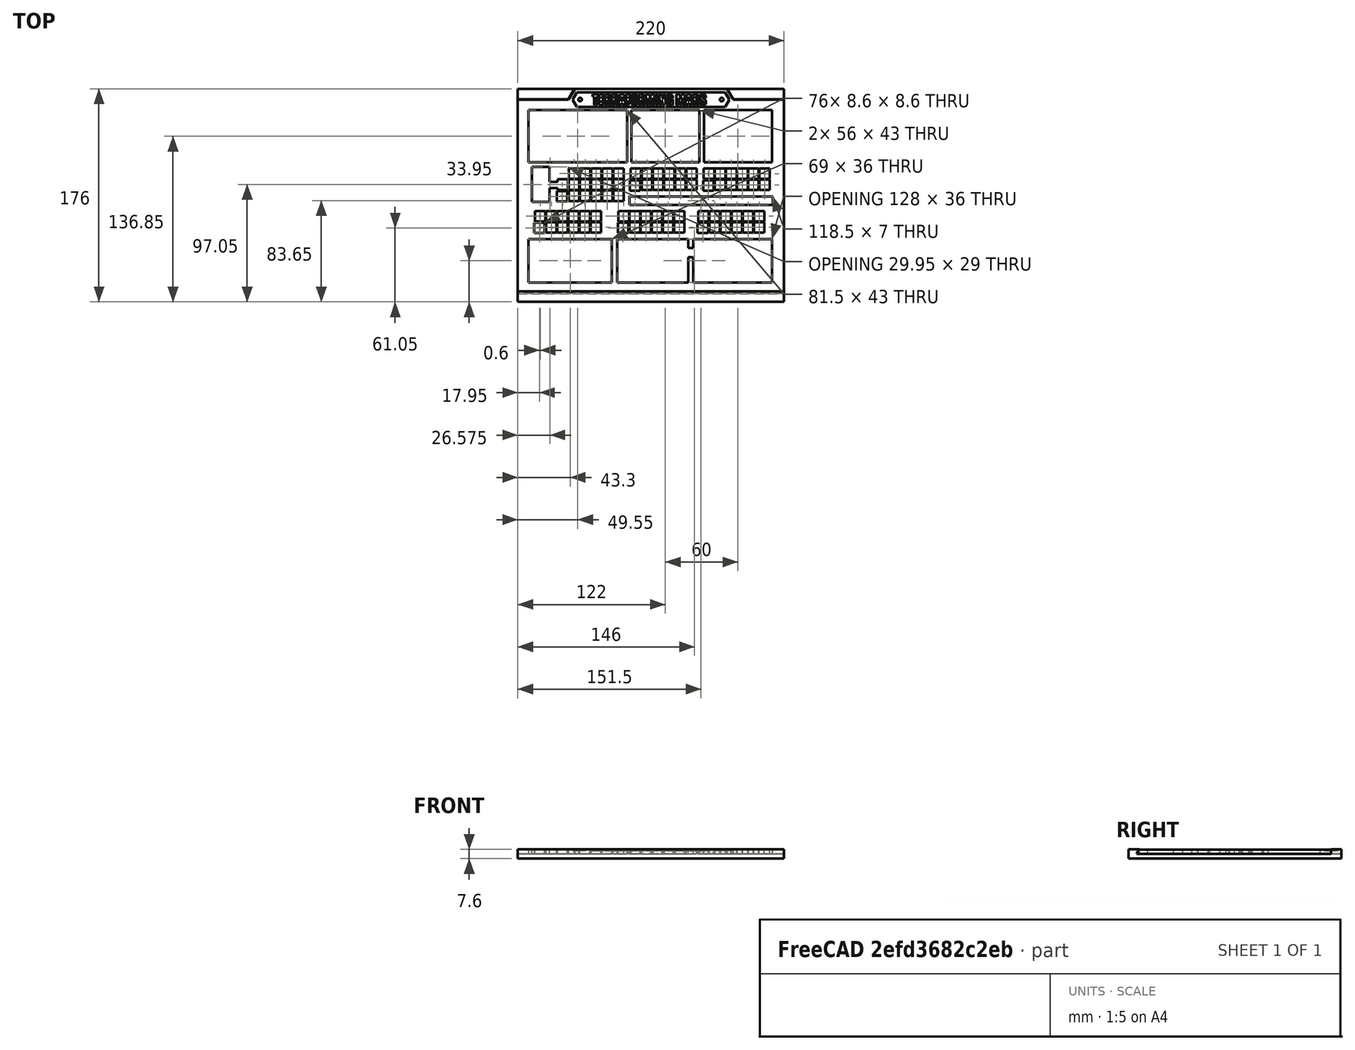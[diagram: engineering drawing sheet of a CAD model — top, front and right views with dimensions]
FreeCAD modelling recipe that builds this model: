
FCSTD DOCUMENT  (FreeCAD 1.0R39109 (Git))
Label: overlay-full-v8
License: All rights reserved
LicenseURL: https://en.wikipedia.org/wiki/All_rights_reserved
objects: Sketcher::SketchObject×11, PartDesign::Pad×9, PartDesign::Pocket×7, Part::Feature×2, PartDesign::Body×2, Mesh::Feature×1, Part::Refine×1, PartDesign::FeatureBase×1, Part::Part2DObjectPython×1, Part::Extrusion×1
note: 79 computed .brp shape members not serialized (recipe doc carries the construction recipe); baked Part::Feature solids carry a one-line shape summary decoded from their .brp

FEATURE [Mesh::Feature] Terraforming_Mars_overlay
FEATURE [Part::Feature] Terraforming_Mars_overlay001
  shape: bbox 208 x 148 x 3.7 mm, 1736 faces, 0 solids (baked)
FEATURE [Part::Feature] Terraforming_Mars_overlay001_solid  label="Terraforming_Mars_overlay001 (Solid)"
  shape: bbox 208 x 148 x 3.7 mm, 1736 faces (baked)
FEATURE [Part::Refine] Terraforming_Mars_overlay001_solid001  label="Terraforming_Mars_overlay001 (Solid)001"
  Source = -> Terraforming_Mars_overlay001_solid
FEATURE [PartDesign::FeatureBase] BaseFeature
  BaseFeature = -> Terraforming_Mars_overlay001_solid001
  Suppressed = false
FEATURE [Sketcher::SketchObject] Sketch
  ArcFitTolerance = 0
  AttachmentSupport = -> [BaseFeature]
  ExternalGeometry = -> [BaseFeature]
  FullyConstrained = true
  MakeInternals = false
  MapMode = 5
  Placement = pos=(0,0,3.7) rot=(0,0,1;0rad)
  sketch-geometry (8):
    g0: LineSegment StartX=6 StartY=154 StartZ=0 EndX=214 EndY=154 EndZ=0
    g1: LineSegment StartX=214 StartY=154 StartZ=0 EndX=214 EndY=6 EndZ=0
    g2: LineSegment StartX=214 StartY=6 StartZ=0 EndX=6 EndY=6 EndZ=0
    g3: LineSegment StartX=6 StartY=6 StartZ=0 EndX=6 EndY=154 EndZ=0
    g4: LineSegment StartX=0 StartY=160 StartZ=0 EndX=220 EndY=160 EndZ=0
    g5: LineSegment StartX=220 StartY=160 StartZ=0 EndX=220 EndY=-0.4 EndZ=0
    g6: LineSegment StartX=220 StartY=-0.4 StartZ=0 EndX=0 EndY=-0.4 EndZ=0
    g7: LineSegment StartX=0 StartY=-0.4 StartZ=0 EndX=0 EndY=160 EndZ=0
  constraints (22):
    c: Coincident(g0,g1)
    c: Coincident(g1,g2)
    c: Coincident(g2,g3)
    c: Coincident(g3,g0)
    c: Horizontal(g0)
    c: Horizontal(g2)
    c: Vertical(g1)
    c: Vertical(g3)
    c: Coincident(g0,g-3)
    c: Coincident(g1,g-4)
    c: Coincident(g4,g5)
    c: Coincident(g5,g6)
    c: Coincident(g6,g7)
    c: Coincident(g7,g4)
    c: Horizontal(g4)
    c: Horizontal(g6)
    c: Vertical(g5)
    c: Vertical(g7)
    c: DistanceX(g4,g0) = 6
    c: DistanceX(g0,g4) = 6
    c: DistanceY(g0,g4) = 6
    c: DistanceY(g5,g1) = 6.4
FEATURE [PartDesign::Pad] Pad
  BaseFeature = -> BaseFeature
  Direction = (0,0,1)
  Length = 10
  Length2 = 10
  Profile = -> Sketch
  ReferenceAxis = -> Sketch [N_Axis]
  Suppressed = false
  Type = 3
  UpToFace = -> BaseFeature [Face1]
FEATURE [Sketcher::SketchObject] Sketch001
  ArcFitTolerance = 0
  AttachmentSupport = -> [Pad]
  ExternalGeometry = -> [Pad]
  FullyConstrained = true
  MakeInternals = false
  MapMode = 5
  Placement = pos=(0,0,3.7) rot=(0,0,1;0rad)
  sketch-geometry (5):
    g0: GeomPoint [constr] X=110 Y=160 Z=0
    g1: LineSegment StartX=42 StartY=160 StartZ=0 EndX=47.0807 EndY=168.8 EndZ=0
    g2: LineSegment StartX=47.0807 StartY=168.8 StartZ=0 EndX=172.919 EndY=168.8 EndZ=0
    g3: LineSegment StartX=172.919 StartY=168.8 StartZ=0 EndX=178 EndY=160 EndZ=0
    g4: LineSegment StartX=178 StartY=160 StartZ=0 EndX=42 EndY=160 EndZ=0
  constraints (13):
    c: Symmetric(g-3,g-3,g0)
    c: Coincident(g1,g2)
    c: Horizontal(g2)
    c: Coincident(g2,g3)
    c: Coincident(g3,g4)
    c: Coincident(g4,g1)
    c: Angle(g1,g4,g1) = 2.0944
    c: Angle(g4,g3,g3) = 2.0944
    c: DistanceY(g1,g1) = 8.8
    c: PointOnObject(g1,g-3)
    c: DistanceX(g-3,g1) = 42
    c: DistanceX(g3,g-3) = 42
    c: PointOnObject(g3,g-3)
FEATURE [PartDesign::Pad] Pad001
  BaseFeature = -> Pad
  Direction = (0,0,1)
  Length = 10
  Length2 = 10
  Profile = -> Sketch001
  ReferenceAxis = -> Sketch001 [N_Axis]
  Suppressed = false
  Type = 3
  UpToFace = -> Pad [Face2]
FEATURE [Sketcher::SketchObject] Sketch002
  ArcFitTolerance = 0
  AttachmentSupport = -> [Pad001]
  ExternalGeometry = -> [Pad001]
  FullyConstrained = true
  MakeInternals = false
  MapMode = 5
  Placement = pos=(0,0,3.7) rot=(0,0,1;0rad)
  sketch-geometry (7):
    g0: GeomPoint [constr] X=110 Y=160 Z=0
    g1: LineSegment StartX=45.2332 StartY=160 StartZ=0 EndX=48.6973 EndY=166 EndZ=0
    g2: LineSegment StartX=48.6973 StartY=166 StartZ=0 EndX=171.303 EndY=166 EndZ=0
    g3: LineSegment StartX=171.303 StartY=166 StartZ=0 EndX=174.767 EndY=160 EndZ=0
    g4: LineSegment StartX=174.767 StartY=160 StartZ=0 EndX=171.303 EndY=154 EndZ=0
    g5: LineSegment StartX=171.303 StartY=154 StartZ=0 EndX=48.6973 EndY=154 EndZ=0
    g6: LineSegment StartX=48.6973 StartY=154 StartZ=0 EndX=45.2332 EndY=160 EndZ=0
  constraints (17):
    c: Symmetric(g-4,g-4,g0)
    c: PointOnObject(g1,g-4)
    c: Coincident(g1,g2)
    c: Horizontal(g2)
    c: Coincident(g2,g3)
    c: PointOnObject(g3,g-4)
    c: Coincident(g3,g4)
    c: PointOnObject(g4,g-5)
    c: Coincident(g4,g5)
    c: Coincident(g5,g6)
    c: Coincident(g6,g1)
    c: Parallel(g1,g-6)
    c: Symmetric(g5,g1,g-4)
    c: Symmetric(g4,g2,g-4)
    c: Parallel(g3,g-7)
    c: Distance(g1,g-6) = 2.8
    c: Distance(g2,g-7) = 2.8
FEATURE [PartDesign::Pocket] Pocket
  BaseFeature = -> Pad001
  Direction = (0,0,-1)
  Length = 1.1
  Length2 = 5
  Profile = -> Sketch002
  ReferenceAxis = -> Sketch002 [N_Axis]
  Suppressed = false
  Type = 0
FEATURE [Part::Part2DObjectPython] ShapeString  # Draft 2D object (typed FeaturePython)
  FontFile = <path>
  Fuse = false
  Justification = 6
  JustificationReference = 0
  KeepLeftMargin = true
  MakeFace = true
  ObliqueAngle = 0
  Placement = pos=(61.7,155.5,2.7) rot=(0,0,1;0rad)
  ScaleToSize = false
  Size = 9
  String = TERRAFORMING MARS
  Tracking = 0
FEATURE [Sketcher::SketchObject] Sketch003
  ArcFitTolerance = 0
  AttachmentSupport = -> [Pocket]
  ExternalGeometry = -> [Pocket]
  FullyConstrained = true
  MakeInternals = false
  MapMode = 5
  Placement = pos=(0,0,2.6) rot=(0,0,1;0rad)
  sketch-geometry (3):
    g0: LineSegment [constr] StartX=42 StartY=160 StartZ=0 EndX=178 EndY=160 EndZ=0
    g1: Circle CenterX=51.5 CenterY=160 CenterZ=0 NormalX=0 NormalY=0 NormalZ=1 AngleXU=0 Radius=1.5
    g2: Circle CenterX=168.5 CenterY=160 CenterZ=0 NormalX=0 NormalY=0 NormalZ=1 AngleXU=0 Radius=1.5
  constraints (8):
    c: Coincident(g0,g-3)
    c: Coincident(g0,g-4)
    c: PointOnObject(g1,g0)
    c: PointOnObject(g2,g0)
    c: Diameter(g2) = 3
    c: Diameter(g1) = 3
    c: DistanceX(g0,g1) = 9.5
    c: DistanceX(g2,g0) = 9.5
FEATURE [PartDesign::Pad] Pad002
  BaseFeature = -> Pocket
  Direction = (0,0,1)
  Length = 1
  Length2 = 10
  Profile = -> Sketch003
  ReferenceAxis = -> Sketch003 [N_Axis]
  Suppressed = false
  Type = 0
FEATURE [Part::Extrusion] Extrude  label="Text"
  Base = -> ShapeString
  Dir = (0,0,1)
  DirMode = 2
  FaceMakerClass = Part::FaceMakerBullseye
  FaceMakerMode = 3
  LengthFwd = 1
  LengthRev = 0
  Placement = pos=(0,0.4,-0.3) rot=(0,0,1;0rad)
  Solid = false
  Symmetric = false
FEATURE [Sketcher::SketchObject] Sketch005
  ArcFitTolerance = 0
  AttachmentSupport = -> [XY_Plane001]
  FullyConstrained = true
  MakeInternals = false
  MapMode = 5
  sketch-geometry (4):
    g0: LineSegment StartX=0 StartY=160.4 StartZ=0 EndX=220 EndY=160.4 EndZ=0
    g1: LineSegment StartX=220 StartY=160.4 StartZ=0 EndX=220 EndY=0 EndZ=0
    g2: LineSegment StartX=220 StartY=0 StartZ=0 EndX=0 EndY=0 EndZ=0
    g3: LineSegment StartX=0 StartY=0 StartZ=0 EndX=0 EndY=160.4 EndZ=0
  constraints (12):
    c: Coincident(g0,g1)
    c: Coincident(g1,g2)
    c: Coincident(g2,g3)
    c: Coincident(g3,g0)
    c: Horizontal(g0)
    c: Horizontal(g2)
    c: Vertical(g1)
    c: Vertical(g3)
    c: PointOnObject(g1,g-1)
    c: PointOnObject(g0,g-2)
    c: DistanceX(g0,g0) = 220
    c: DistanceY(g1,g1) = 160.4
FEATURE [PartDesign::Pad] Pad004
  Direction = (0,0,1)
  Length = 4
  Length2 = 10
  Profile = -> Sketch005
  ReferenceAxis = -> Sketch005 [N_Axis]
  Reversed = true
  Suppressed = false
  Type = 0
FEATURE [PartDesign::Pad] Pad005
  BaseFeature = -> Pad004
  Direction = (0,-1,0)
  Length = 6.8
  Length2 = 10
  Profile = -> Pad004 [Face3]
  Suppressed = false
  Type = 0
FEATURE [PartDesign::Pad] Pad006
  BaseFeature = -> Pad005
  Direction = (0,0,1)
  Length = 3.6
  Length2 = 10
  Profile = -> Pad005 [Face8]
  Suppressed = false
  Type = 0
FEATURE [PartDesign::Pad] Pad007
  BaseFeature = -> Pad006
  Direction = (0,1,0)
  Length = 2
  Length2 = 10
  Profile = -> Pad006 [Face8]
  Suppressed = false
  Type = 0
FEATURE [Sketcher::SketchObject] Sketch006
  ArcFitTolerance = 0
  AttachmentSupport = -> [Pad007]
  ExternalGeometry = -> [Pad007]
  FullyConstrained = true
  MakeInternals = false
  MapMode = 5
  Placement = pos=(220,0,0) rot=(0.57735,0.57735,0.57735;2.0944rad)
  sketch-geometry (4):
    g0: LineSegment StartX=-0.1 StartY=0 StartZ=0 EndX=2 EndY=0 EndZ=0
    g1: LineSegment StartX=2 StartY=0 StartZ=0 EndX=2 EndY=3.6 EndZ=0
    g2: LineSegment StartX=-0.1 StartY=0 StartZ=0 EndX=1.9 EndY=3.6 EndZ=0
    g3: LineSegment StartX=1.9 StartY=3.6 StartZ=0 EndX=2 EndY=3.6 EndZ=0
  constraints (10):
    c: PointOnObject(g0,g-1)
    c: Coincident(g0,g-5)
    c: Coincident(g1,g0)
    c: DistanceX(g0,g0) = 2.1
    c: Coincident(g2,g0)
    c: PointOnObject(g2,g-4)
    c: Coincident(g3,g2)
    c: Coincident(g3,g1)
    c: DistanceX(g3,g3) = 0.1
    c: Coincident(g1,g-5)
FEATURE [PartDesign::Pocket] Pocket002
  BaseFeature = -> Pad007
  Direction = (-1,0,0)
  Length = 5
  Length2 = 5
  Profile = -> Sketch006
  ReferenceAxis = -> Sketch006 [N_Axis]
  Suppressed = false
  Type = 1
FEATURE [PartDesign::Pad] Pad008
  BaseFeature = -> Pocket002
  Direction = (0,1,0)
  Length = 8.8
  Length2 = 10
  Profile = -> Pocket002 [Face1]
  Suppressed = false
  Type = 0
FEATURE [Sketcher::SketchObject] Sketch007
  ArcFitTolerance = 0
  AttachmentSupport = -> [Pad008]
  ExternalGeometry = -> [Pad008]
  FullyConstrained = true
  MakeInternals = false
  MapMode = 5
  sketch-geometry (12):
    g0: LineSegment [constr] StartX=47.0807 StartY=169.2 StartZ=0 EndX=42 EndY=160.4 EndZ=0
    g1: LineSegment [constr] StartX=42 StartY=160.4 StartZ=0 EndX=0 EndY=160.4 EndZ=0
    g2: LineSegment StartX=0 StartY=169.2 StartZ=0 EndX=0 EndY=160.5 EndZ=0
    g3: LineSegment StartX=0 StartY=160.5 StartZ=0 EndX=41.9423 EndY=160.5 EndZ=0
    g4: LineSegment StartX=41.9423 StartY=160.5 StartZ=0 EndX=46.9652 EndY=169.2 EndZ=0
    g5: LineSegment StartX=46.9652 StartY=169.2 StartZ=0 EndX=0 EndY=169.2 EndZ=0
    g6: LineSegment [constr] StartX=220 StartY=160.4 StartZ=0 EndX=178 EndY=160.4 EndZ=0
    g7: LineSegment [constr] StartX=172.919 StartY=169.2 StartZ=0 EndX=178 EndY=160.4 EndZ=0
    g8: LineSegment StartX=173.035 StartY=169.2 StartZ=0 EndX=220 EndY=169.2 EndZ=0
    g9: LineSegment StartX=220 StartY=169.2 StartZ=0 EndX=220 EndY=160.5 EndZ=0
    g10: LineSegment StartX=220 StartY=160.5 StartZ=0 EndX=178.058 EndY=160.5 EndZ=0
    g11: LineSegment StartX=178.058 StartY=160.5 StartZ=0 EndX=173.035 EndY=169.2 EndZ=0
  constraints (34):
    c: PointOnObject(g0,g-4)
    c: PointOnObject(g0,g-3)
    c: Coincident(g0,g1)
    c: Coincident(g1,g-3)
    c: DistanceX(g1,g1) = 42
    c: Angle(g0,g-3,g0) = 2.0944
    c: Coincident(g-4,g2)
    c: PointOnObject(g2,g-2)
    c: Coincident(g2,g3)
    c: Horizontal(g3)
    c: Coincident(g3,g4)
    c: PointOnObject(g4,g-4)
    c: Coincident(g4,g5)
    c: Coincident(g5,g2)
    c: Distance(g2,g1) = 0.1
    c: Distance(g4,g0) = 0.1
    c: Parallel(g4,g0)
    c: Coincident(g6,g-3)
    c: PointOnObject(g6,g-3)
    c: PointOnObject(g7,g-4)
    c: Coincident(g7,g6)
    c: DistanceX(g6,g6) = 42
    c: Angle(g7,g-3,g6) = 1.0472
    c: PointOnObject(g8,g-4)
    c: Coincident(g8,g-4)
    c: Coincident(g8,g9)
    c: Vertical(g9)
    c: Coincident(g9,g10)
    c: Horizontal(g10)
    c: Coincident(g10,g11)
    c: Coincident(g11,g8)
    c: Distance(g9,g6) = 0.1
    c: Distance(g8,g7) = 0.1
    c: Parallel(g11,g7)
FEATURE [PartDesign::Pad] Pad009
  BaseFeature = -> Pad008
  Direction = (0,0,1)
  Length = 3.6
  Length2 = 10
  Profile = -> Sketch007
  ReferenceAxis = -> Sketch007 [N_Axis]
  Suppressed = false
  Type = 0
FEATURE [Sketcher::SketchObject] Sketch008
  ArcFitTolerance = 0
  AttachmentSupport = -> [Pad009]
  ExternalGeometry = -> [Pad009]
  FullyConstrained = true
  MakeInternals = false
  MapMode = 5
  sketch-geometry (4):
    g0: LineSegment StartX=0 StartY=0 StartZ=0 EndX=220 EndY=0 EndZ=0
    g1: LineSegment StartX=220 StartY=0 StartZ=0 EndX=220 EndY=160.4 EndZ=0
    g2: LineSegment StartX=220 StartY=160.4 StartZ=0 EndX=0 EndY=160.4 EndZ=0
    g3: LineSegment StartX=0 StartY=160.4 StartZ=0 EndX=0 EndY=0 EndZ=0
  constraints (10):
    c: Coincident(g0,g1)
    c: Coincident(g1,g2)
    c: Coincident(g2,g3)
    c: Coincident(g3,g0)
    c: Horizontal(g0)
    c: Horizontal(g2)
    c: Vertical(g1)
    c: Vertical(g3)
    c: Coincident(g0,g-1)
    c: Coincident(g1,g-3)
FEATURE [PartDesign::Pocket] Pocket003
  BaseFeature = -> Pad009
  Direction = (0,0,-1)
  Length = 0.2
  Length2 = 5
  Profile = -> Sketch008
  ReferenceAxis = -> Sketch008 [N_Axis]
  Suppressed = false
  Type = 0
FEATURE [Sketcher::SketchObject] Sketch009
  ArcFitTolerance = 0
  AttachmentSupport = -> [Pad002]
  ExternalGeometry = -> [Pad002]
  FullyConstrained = true
  MakeInternals = false
  MapMode = 5
  Placement = pos=(220,0,0) rot=(0.57735,0.57735,0.57735;2.0944rad)
  sketch-geometry (3):
    g0: LineSegment StartX=1.6 StartY=3.7 StartZ=0 EndX=-0.4 EndY=0 EndZ=0
    g1: LineSegment StartX=1.6 StartY=3.7 StartZ=0 EndX=-0.4 EndY=3.7 EndZ=0
    g2: LineSegment StartX=-0.4 StartY=3.7 StartZ=0 EndX=-0.4 EndY=0 EndZ=0
  constraints (8):
    c: PointOnObject(g0,g-3)
    c: Coincident(g1,g0)
    c: Coincident(g1,g-4)
    c: Coincident(g2,g1)
    c: Coincident(g2,g0)
    c: Vertical(g2)
    c: DistanceX(g1,g1) = 2
    c: PointOnObject(g0,g-1)
FEATURE [PartDesign::Pocket] Pocket004
  BaseFeature = -> Pad002
  Direction = (-1,0,0)
  Length = 5
  Length2 = 5
  Profile = -> Sketch009
  ReferenceAxis = -> Sketch009 [N_Axis]
  Suppressed = false
  Type = 1
FEATURE [Sketcher::SketchObject] Sketch010
  ArcFitTolerance = 0
  AttachmentSupport = -> [Pocket004]
  ExternalGeometry = -> [Pocket004]
  FullyConstrained = true
  MakeInternals = false
  MapMode = 5
  Placement = pos=(0,0,3.7) rot=(0,0,1;0rad)
  sketch-geometry (4):
    g0: LineSegment StartX=0 StartY=0 StartZ=0 EndX=220 EndY=0 EndZ=0
    g1: LineSegment StartX=220 StartY=0 StartZ=0 EndX=220 EndY=168.8 EndZ=0
    g2: LineSegment StartX=220 StartY=168.8 StartZ=0 EndX=0 EndY=168.8 EndZ=0
    g3: LineSegment StartX=0 StartY=168.8 StartZ=0 EndX=0 EndY=0 EndZ=0
  constraints (11):
    c: Coincident(g0,g1)
    c: Coincident(g1,g2)
    c: Coincident(g2,g3)
    c: Coincident(g3,g0)
    c: Horizontal(g0)
    c: Horizontal(g2)
    c: Vertical(g1)
    c: Vertical(g3)
    c: Coincident(g0,g-1)
    c: PointOnObject(g-3,g2)
    c: PointOnObject(g-4,g1)
FEATURE [PartDesign::Pocket] Pocket005
  BaseFeature = -> Pocket004
  Direction = (0,0,-1)
  Length = 0.1
  Length2 = 5
  Profile = -> Sketch010
  ReferenceAxis = -> Sketch010 [N_Axis]
  Suppressed = false
  Type = 0
FEATURE [PartDesign::Pocket] Pocket006
  BaseFeature = -> Pocket003
  Direction = (0,0,-1)
  Length = 0
  Length2 = 5
  Profile = -> Pocket003 [Face2]
  Refine = true
  Suppressed = false
  Type = 3
  UpToFace = -> Pocket003 [Face16]
FEATURE [PartDesign::Body] Body001  label="Back"
  AllowCompound = false
  Group = -> [Sketch005,Pad004,Pad005,Pad006,Pad007,Sketch006,Pocket002,Pad008,Sketch007,Pad009,Sketch008,Pocket003,Pocket006]
  Origin = -> Origin001
  Tip = -> Pocket006
FEATURE [Sketcher::SketchObject] Sketch011
  ArcFitTolerance = 1e-06
  AttachmentSupport = -> [Pocket005]
  ExternalGeometry = -> [Pocket005]
  FullyConstrained = true
  MakeInternals = false
  MapMode = 5
  Placement = pos=(0,0,0) rot=(1,0,0;3.14159rad)
  sketch-geometry (4):
    g0: LineSegment StartX=0 StartY=0.4 StartZ=0 EndX=0 EndY=-168.8 EndZ=0
    g1: LineSegment StartX=0 StartY=-168.8 StartZ=0 EndX=220 EndY=-168.8 EndZ=0
    g2: LineSegment StartX=220 StartY=-168.8 StartZ=0 EndX=220 EndY=0.4 EndZ=0
    g3: LineSegment StartX=220 StartY=0.4 StartZ=0 EndX=0 EndY=0.4 EndZ=0
  constraints (11):
    c: Coincident(g0,g1)
    c: Coincident(g1,g2)
    c: Coincident(g2,g3)
    c: Vertical(g0)
    c: Vertical(g2)
    c: Horizontal(g1)
    c: Horizontal(g3)
    c: PointOnObject(g-4,g1)
    c: PointOnObject(g-3,g2)
    c: Coincident(g0,g-5)
    c: Coincident(g3,g0)
FEATURE [PartDesign::Pocket] Pocket007
  BaseFeature = -> Pocket005
  Direction = (0,0,1)
  Length = 0.2
  Length2 = 5
  Profile = -> Sketch011
  ReferenceAxis = -> Sketch011 [N_Axis]
  Refine = true
  Suppressed = false
  Type = 0
FEATURE [PartDesign::Body] Body  label="Front"
  AllowCompound = false
  BaseFeature = -> Terraforming_Mars_overlay001_solid001
  Group = -> [BaseFeature,Sketch,Pad,Sketch001,Pad001,Sketch002,Pocket,Sketch003,Pad002,Sketch009,Pocket004,Sketch010,Pocket005,Sketch011,Pocket007]
  Origin = -> Origin
  Placement = pos=(0,0.35,-0.2) rot=(0,0,1;0rad)
  Tip = -> Pocket007
note: 1 file-system path scrubbed to <path> (originals preserved in the JSON sidecar)
